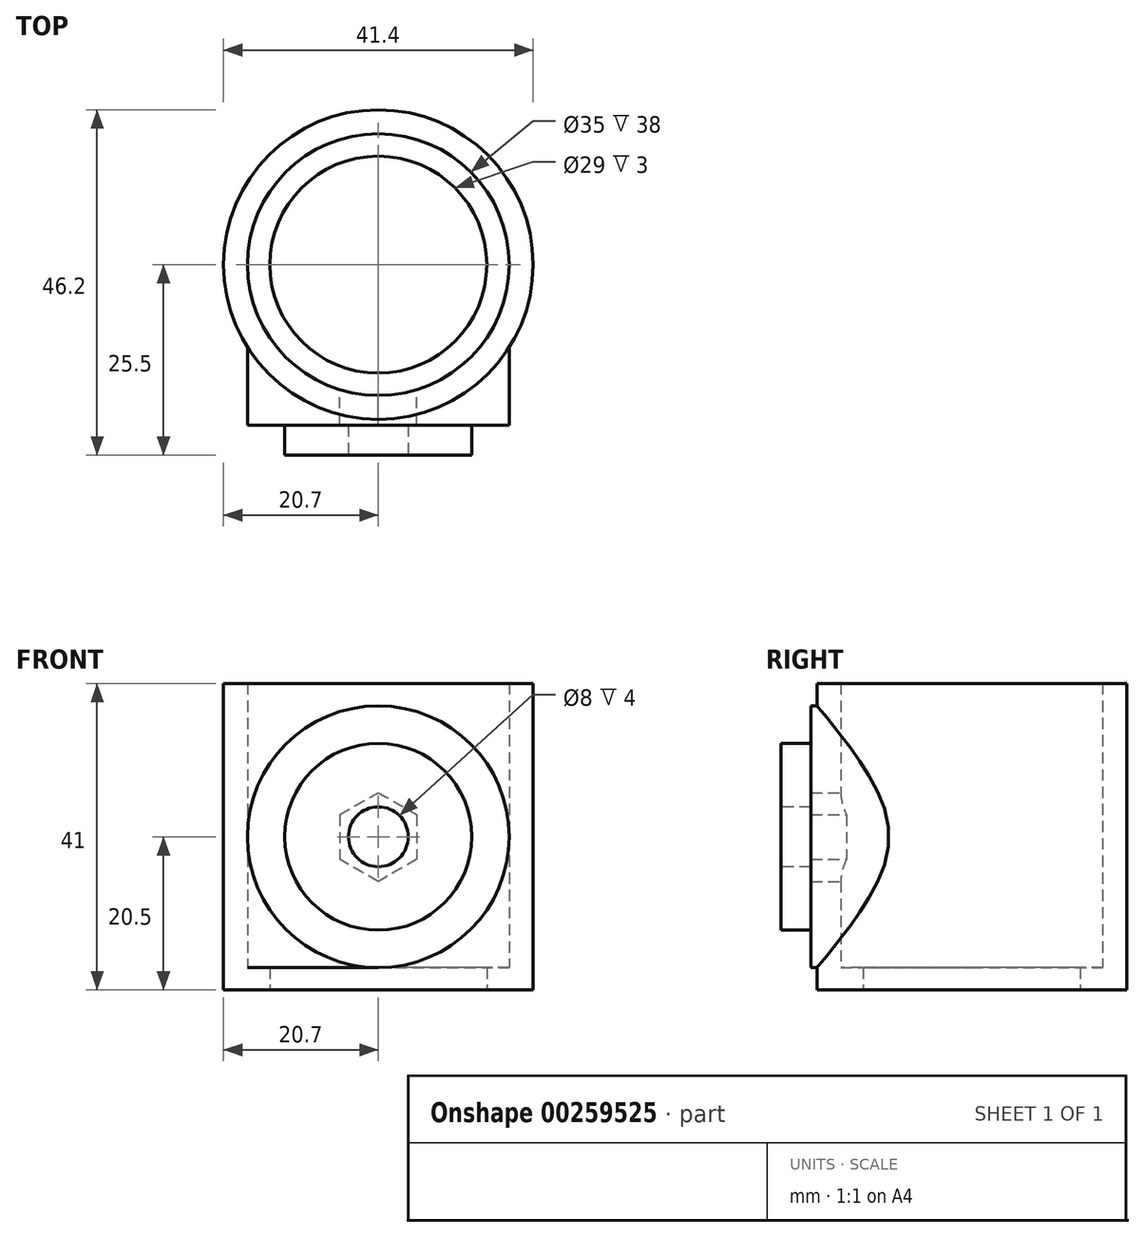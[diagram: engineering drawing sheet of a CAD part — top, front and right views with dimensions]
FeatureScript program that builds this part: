
annotation { "Feature Type Name" : "Feature", "Feature Type Description" : "" }
export const myFeature = defineFeature(function(context is Context, id is Id, definition is map)
    precondition{}
    {
        {
            var Q0;
            Q0=qCreatedBy(makeId("Top.planeOp"),FACE);
            var sketch = newSketch(context, id + "F0", { "sketchPlane" : qUnion([Q0])});
            skCircle(sketch, "E0", {"center": v(0, 0) * mm, "radius": 17.5 * mm});
            skCircle(sketch, "E1.0", {"center": v(0, 0) * mm, "radius": 20.7 * mm});
            skCircle(sketch, "E2.0", {"center": v(0, 0) * mm, "radius": 14.5 * mm});
            skSolve(sketch);
        }
        {
            var Q0;
            Q0=makeQuery(id+"F0.imprint","IMPRINT",FACE,{"disambiguationData":[TD([[makeQuery(id+"F0.imprint","IMPRINT",EDGE,{"derivedFrom":sQuery(id+"F0.wireOp",EDGE,"E0")}),-1.0]])]});
            extrude(context, id + "F1", {"entities" : qUnion([Q0]), "depth" : 41 * mm});
        }
        {
            var Q0;
            Q0=makeQuery(id+"F0.imprint","IMPRINT",FACE,{"disambiguationData":[TD([[makeQuery(id+"F0.imprint","IMPRINT",EDGE,{"derivedFrom":sQuery(id+"F0.wireOp",EDGE,"E0")}),1.0]])]});
            extrude(context, id + "F2", {"entities" : qUnion([Q0]), "operationType" : NewBodyOperationType.ADD, "depth" : 3 * mm});
        }
        {
            var Q0;
            Q0=qCreatedBy(makeId("Front.planeOp"),FACE);
            cPlane(context, id + "F3", {"entities" : qUnion([Q0]), "cplaneType" : CPlaneType.OFFSET, "offset" : 25.5 * mm, "width" : 150 * mm, "height" : 150 * mm});
        }
        {
            var Q0;
            Q0=qCreatedBy(id+"F3.planeOp",FACE);
            var sketch = newSketch(context, id + "F4", { "sketchPlane" : qUnion([Q0])});
            skCircle(sketch, "E3", {"center": v(0, 20.5) * mm, "radius": 17.5 * mm});
            skCircle(sketch, "E4", {"center": v(0, 20.5) * mm, "radius": 12.5 * mm});
            skCircle(sketch, "E5", {"center": v(0, 20.5) * mm, "radius": 4 * mm});
            skSolve(sketch);
        }
        {
            var Q0;
            Q0=makeQuery(id+"F4.imprint","IMPRINT",FACE,{"disambiguationData":[TD([[makeQuery(id+"F4.imprint","IMPRINT",EDGE,{"derivedFrom":sQuery(id+"F4.wireOp",EDGE,"E3")}),1.0]])]});
            var Q1;
            Q1=makeQuery(id+"F4.imprint","IMPRINT",FACE,{"disambiguationData":[TD([[makeQuery(id+"F4.imprint","IMPRINT",EDGE,{"derivedFrom":sQuery(id+"F4.wireOp",EDGE,"E4")}),1.0]])]});
            extrude(context, id + "F5", {"entities" : qUnion([Q0, Q1]), "operationType" : NewBodyOperationType.ADD, "endBound" : BoundingType.UP_TO_NEXT, "oppositeDirection" : true, "depth" : 25 * mm});
        }
        {
            var Q0;
            Q0=makeQuery(id+"F4.imprint","IMPRINT",FACE,{"disambiguationData":[TD([[makeQuery(id+"F4.imprint","IMPRINT",EDGE,{"derivedFrom":sQuery(id+"F4.wireOp",EDGE,"E3")}),1.0]])]});
            extrude(context, id + "F6", {"entities" : qUnion([Q0]), "operationType" : NewBodyOperationType.REMOVE, "oppositeDirection" : true, "depth" : 4 * mm});
        }
        {
            var Q0;
            Q0=makeQuery(id+"F4.imprint","IMPRINT",FACE,{"disambiguationData":[TD([[makeQuery(id+"F4.imprint","IMPRINT",EDGE,{"derivedFrom":sQuery(id+"F4.wireOp",EDGE,"E5")}),1.0]])]});
            var Q1;
            Q1=sQuery(id+"F4.wireOp",EDGE,"E5");
            extrude(context, id + "F7", {"entities" : qUnion([Q0]), "operationType" : NewBodyOperationType.REMOVE, "surfaceEntities" : qUnion([Q1]), "oppositeDirection" : true, "depth" : 25 * mm});
        }
        {
            var Q0;
            Q0=qCreatedBy(makeId("Front.planeOp"),FACE);
            var sketch = newSketch(context, id + "F8", { "sketchPlane" : qUnion([Q0])});
            skCircle(sketch, "E6.cCircle", {"center": v(0, 20.46) * mm, "radius": 5.15 * mm, "construction": true});
            skLineSegment(sketch, "E6.0", {"start": v(0, 26.4) * mm, "end": v(5.15, 23.44) * mm});
            skLineSegment(sketch, "E6.1", {"start": v(5.15, 23.44) * mm, "end": v(5.15, 17.49) * mm});
            skLineSegment(sketch, "E6.2", {"start": v(5.15, 17.49) * mm, "end": v(0, 14.52) * mm});
            skLineSegment(sketch, "E6.3", {"start": v(0, 14.52) * mm, "end": v(-5.15, 17.49) * mm});
            skLineSegment(sketch, "E6.4", {"start": v(-5.15, 17.49) * mm, "end": v(-5.15, 23.44) * mm});
            skLineSegment(sketch, "E6.5", {"start": v(-5.15, 23.44) * mm, "end": v(0, 26.4) * mm});
            skPoint(sketch, "E6.0.midPoint", {"position": v(2.57, 24.92) * mm});
            skSolve(sketch);
        }
        {
            var Q0;
            Q0 = qSketchRegion(id + "F8", true);
            var Q1;
            Q1=makeQuery(id+"F6.boolean.opBoolean","COPY",FACE,{"derivedFrom":makeQuery(id+"F6.opExtrude","CAP_FACE",FACE,{"disambiguationData":[OSD([sQuery(id+"F4.wireOp",EDGE,"E3"),sQuery(id+"F4.wireOp",EDGE,"E4")])],"isStart":false})});
            extrude(context, id + "F9", {"entities" : qUnion([Q0]), "operationType" : NewBodyOperationType.REMOVE, "endBound" : BoundingType.UP_TO_SURFACE, "endBoundEntityFace" : qUnion([Q1]), "depth" : 21 * mm});
        }
    });
